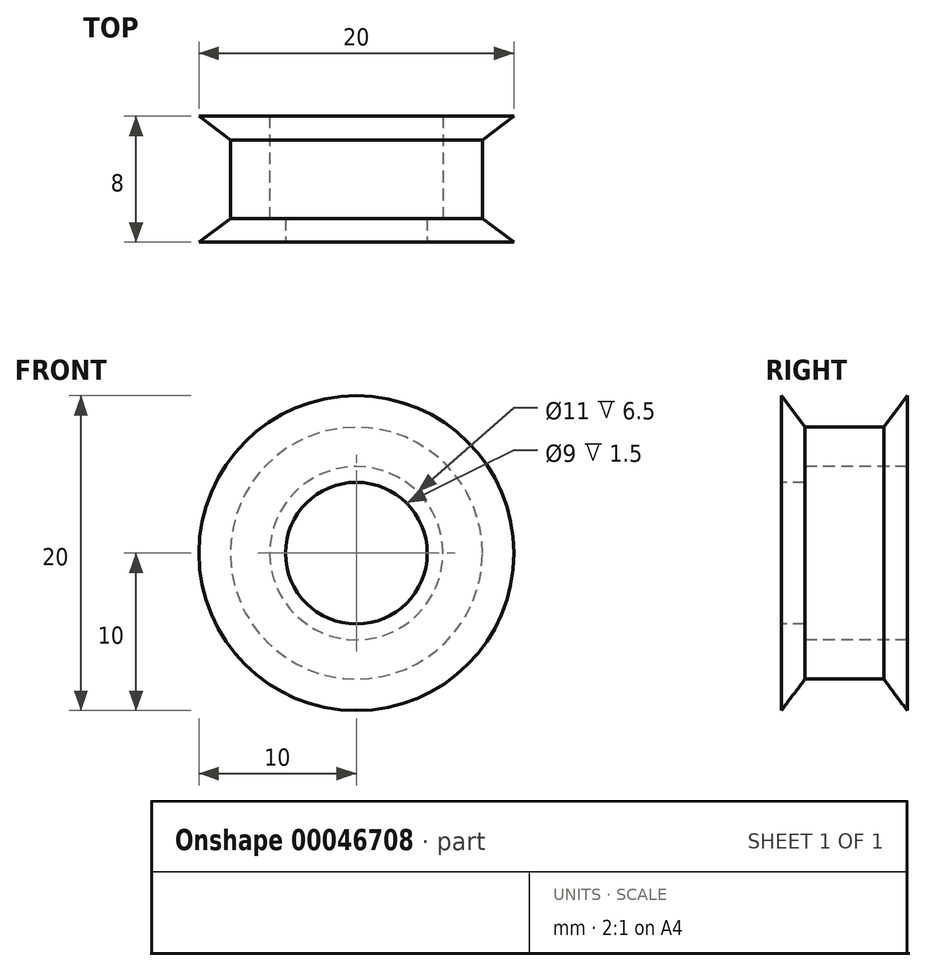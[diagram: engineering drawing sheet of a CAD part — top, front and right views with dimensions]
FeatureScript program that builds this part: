
annotation { "Feature Type Name" : "Feature", "Feature Type Description" : "" }
export const myFeature = defineFeature(function(context is Context, id is Id, definition is map)
    precondition{}
    {
        {
            var Q0;
            Q0=qCreatedBy(makeId("Right.planeOp"),FACE);
            var sketch = newSketch(context, id + "F0", { "sketchPlane" : qUnion([Q0])});
            skLineSegment(sketch, "E0", {"start": v(0, 0) * mm, "end": v(38.44, 0) * mm, "construction": true});
            skLineSegment(sketch, "E1", {"start": v(-2.5, 8) * mm, "end": v(2.5, 8) * mm});
            skLineSegment(sketch, "E2", {"start": v(2.5, 8) * mm, "end": v(4, 10) * mm});
            skLineSegment(sketch, "E3", {"start": v(4, 10) * mm, "end": v(4, 5.5) * mm});
            skLineSegment(sketch, "E4", {"start": v(4, 5.5) * mm, "end": v(-4, 5.5) * mm});
            skLineSegment(sketch, "E5", {"start": v(-4, 5.5) * mm, "end": v(-4, 10) * mm});
            skLineSegment(sketch, "E6", {"start": v(-4, 10) * mm, "end": v(-2.5, 8) * mm});
            skSolve(sketch);
        }
        {
            var Q0;
            Q0=makeQuery(id+"F0.imprint","IMPRINT",FACE,{"disambiguationData":[TD([[makeQuery(id+"F0.imprint","IMPRINT",EDGE,{"derivedFrom":sQuery(id+"F0.wireOp",EDGE,"E1")}),-1.0]])]});
            var Q1;
            Q1=sQuery(id+"F0.wireOp",EDGE,"E0");
            revolve(context, id + "F1", {"surfaceOperationType" : NewSurfaceOperationType.NEW, "entities" : qUnion([Q0]), "axis" : qUnion([Q1]), "revolveType" : RevolveType.FULL});
        }
        {
            var Q0;
            Q0=makeQuery(id+"F1.opRevolve","SWEPT_FACE",FACE,{"disambiguationData":[OSD([sQuery(id+"F0.wireOp",EDGE,"E5")])]});
            var sketch = newSketch(context, id + "F2", { "sketchPlane" : qUnion([Q0])});
            skCircle(sketch, "E7", {"center": v(0, 0) * mm, "radius": 4.5 * mm});
            skCircle(sketch, "E8.0", {"center": v(0, 0) * mm, "radius": 5.5 * mm});
            skSolve(sketch);
        }
        {
            var Q0;
            Q0=makeQuery(id+"F2.imprint","IMPRINT",FACE,{"disambiguationData":[TD([[makeQuery(id+"F2.imprint","IMPRINT",EDGE,{"derivedFrom":sQuery(id+"F2.wireOp",EDGE,"E7")}),-1.0]])]});
            extrude(context, id + "F3", {"entities" : qUnion([Q0]), "operationType" : NewBodyOperationType.ADD, "oppositeDirection" : true, "depth" : 1.5 * mm, "offsetDistance" : 25 * mm});
        }
    });
